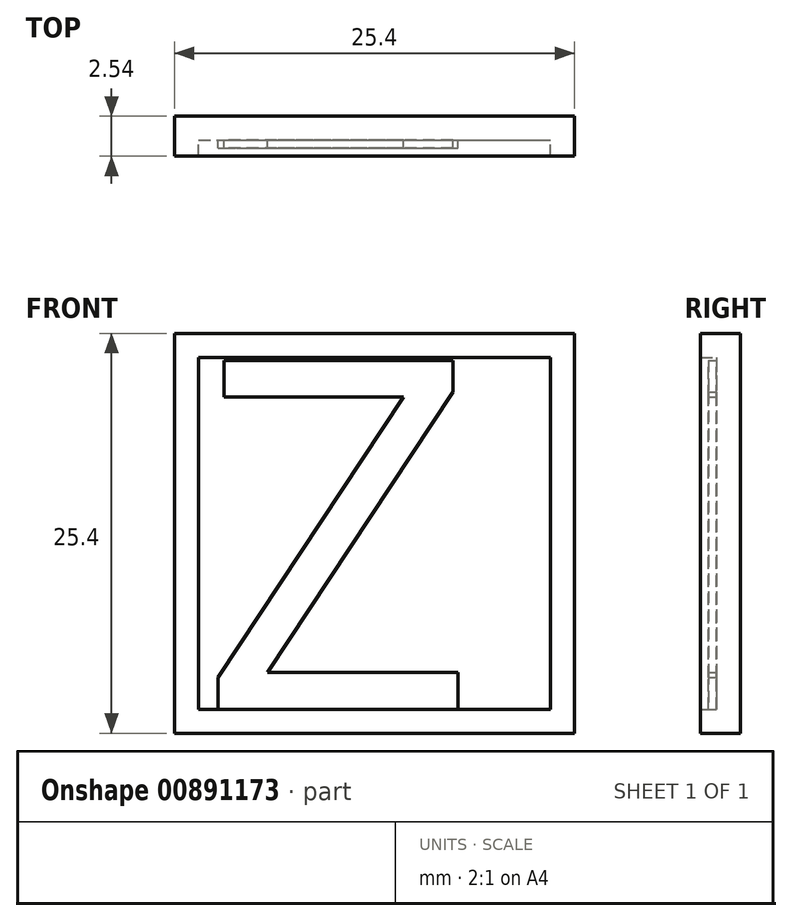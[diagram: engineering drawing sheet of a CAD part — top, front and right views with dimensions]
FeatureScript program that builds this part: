
annotation { "Feature Type Name" : "Feature", "Feature Type Description" : "" }
export const myFeature = defineFeature(function(context is Context, id is Id, definition is map)
    precondition{}
    {
        {
            var Q0;
            Q0=qCreatedBy(makeId("Front.planeOp"),FACE);
            var sketch = newSketch(context, id + "F0", { "sketchPlane" : qUnion([Q0])});
            skLineSegment(sketch, "E0.bottom", {"start": v(-24.47, -1.4) * mm, "end": v(0.93, -1.4) * mm});
            skLineSegment(sketch, "E0.top", {"start": v(-24.47, -26.8) * mm, "end": v(0.93, -26.8) * mm});
            skLineSegment(sketch, "E0.left", {"start": v(-24.47, -1.4) * mm, "end": v(-24.47, -26.8) * mm});
            skLineSegment(sketch, "E0.right", {"start": v(0.93, -1.4) * mm, "end": v(0.93, -26.8) * mm});
            skSolve(sketch);
        }
        {
            var Q0;
            Q0=makeQuery(id+"F0.imprint","IMPRINT",FACE,{"disambiguationData":[TD([[makeQuery(id+"F0.imprint","IMPRINT",EDGE,{"derivedFrom":sQuery(id+"F0.wireOp",EDGE,"E0.bottom")}),-1.0]])]});
            extrude(context, id + "F1", {"entities" : qUnion([Q0]), "depth" : 2.54 * mm, "offsetDistance" : 25.4 * mm});
        }
        {
            var Q0;
            Q0=makeQuery(id+"F1.opExtrude","CAP_FACE",FACE,{"disambiguationData":[OSD([sQuery(id+"F0.wireOp",EDGE,"E0.bottom"),sQuery(id+"F0.wireOp",EDGE,"E0.top"),sQuery(id+"F0.wireOp",EDGE,"E0.left"),sQuery(id+"F0.wireOp",EDGE,"E0.right")])],"isStart":false});
            shell(context, id + "F2", {"entities" : qUnion([Q0]), "thickness" : 1.52 * mm});
        }
        {
            var Q0;
            Q0=makeQuery(id+"F2.opShell","OFFSET_FACE",FACE,{"disambiguationData":[OSD([sQuery(id+"F0.wireOp",EDGE,"E0.bottom"),sQuery(id+"F0.wireOp",EDGE,"E0.top"),sQuery(id+"F0.wireOp",EDGE,"E0.left"),sQuery(id+"F0.wireOp",EDGE,"E0.right")])]});
            var sketch = newSketch(context, id + "F3", { "sketchPlane" : qUnion([Q0])});
            skText(sketch, "E1", { "text": "Z", "fontName": "OpenSans-Regular.ttf"});
            const initialGuessF3  = {"E1": [-0.02294, -0.02527, 1, 0, 0.02235]};
            skSetInitialGuess(sketch, initialGuessF3);
            skSolve(sketch);
        }
        {
            var Q0;
            Q0 = qSketchRegion(id + "F3", true);
            extrude(context, id + "F4", {"entities" : qUnion([Q0]), "operationType" : NewBodyOperationType.ADD, "depth" : 0.5 * mm, "offsetDistance" : 25.4 * mm});
        }
    });
